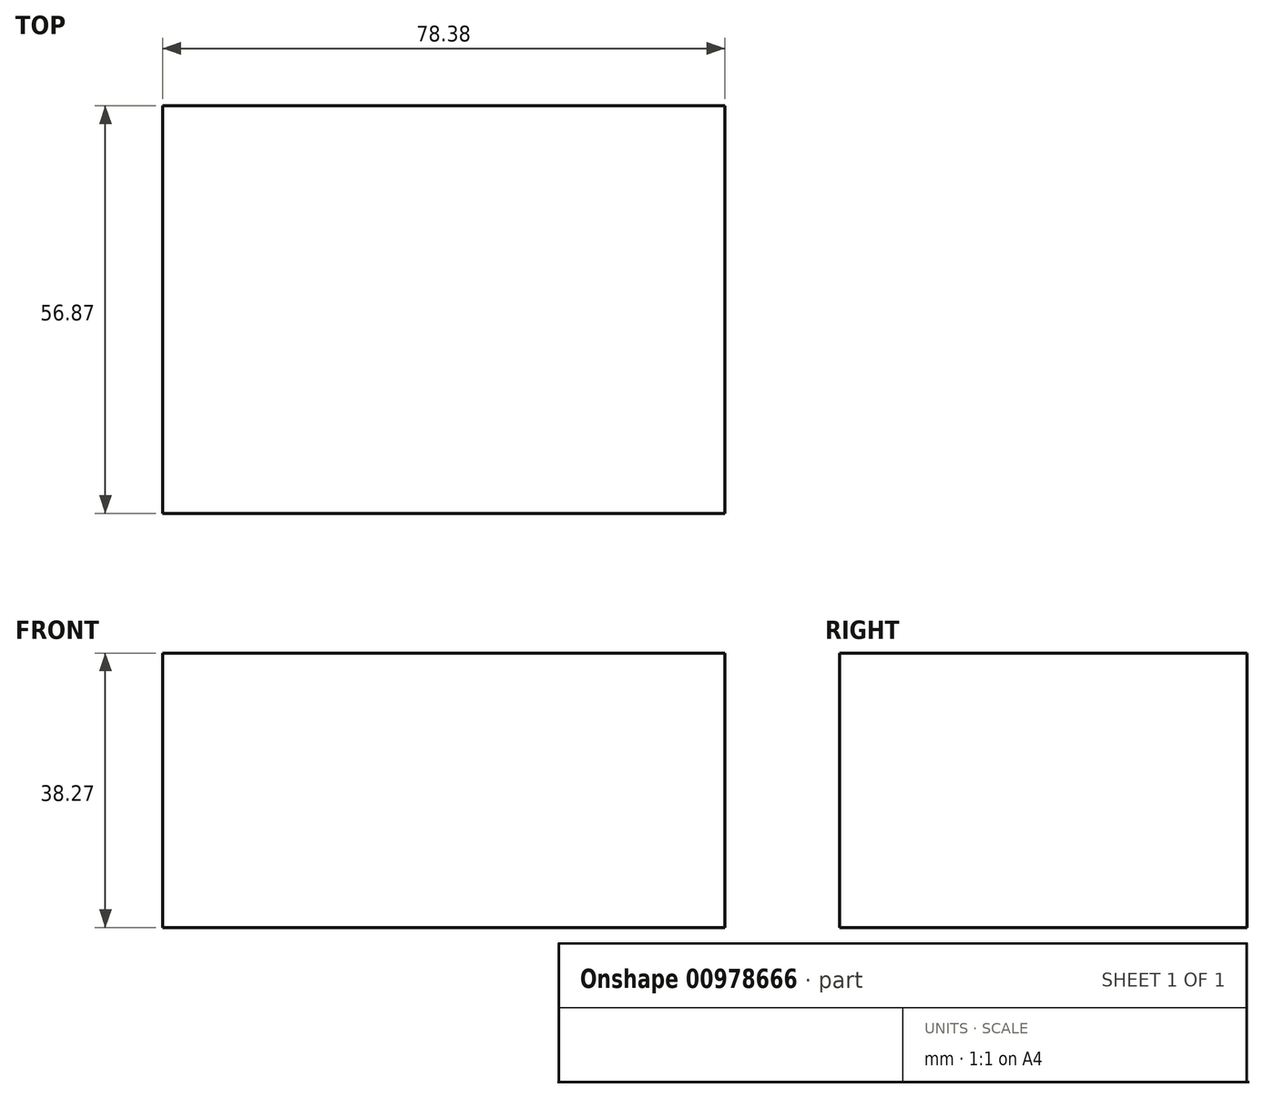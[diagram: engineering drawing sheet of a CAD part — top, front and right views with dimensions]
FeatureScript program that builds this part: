
annotation { "Feature Type Name" : "Feature", "Feature Type Description" : "" }
export const myFeature = defineFeature(function(context is Context, id is Id, definition is map)
    precondition{}
    {
        {
            var Q0;
            Q0=qCreatedBy(makeId("Front.planeOp"),FACE);
            var sketch = newSketch(context, id + "F0", { "sketchPlane" : qUnion([Q0])});
            skLineSegment(sketch, "E0.bottom", {"start": v(-33.82, 0) * mm, "end": v(44.56, 0) * mm});
            skLineSegment(sketch, "E0.top", {"start": v(-33.82, 38.27) * mm, "end": v(44.56, 38.27) * mm});
            skLineSegment(sketch, "E0.left", {"start": v(-33.82, 0) * mm, "end": v(-33.82, 38.27) * mm});
            skLineSegment(sketch, "E0.right", {"start": v(44.56, 0) * mm, "end": v(44.56, 38.27) * mm});
            skSolve(sketch);
        }
        {
            var Q0;
            Q0 = qSketchRegion(id + "F0", true);
            extrude(context, id + "F1", {"entities" : qUnion([Q0]), "depth" : 56.87 * mm, "offsetDistance" : 25.4 * mm});
        }
    });
